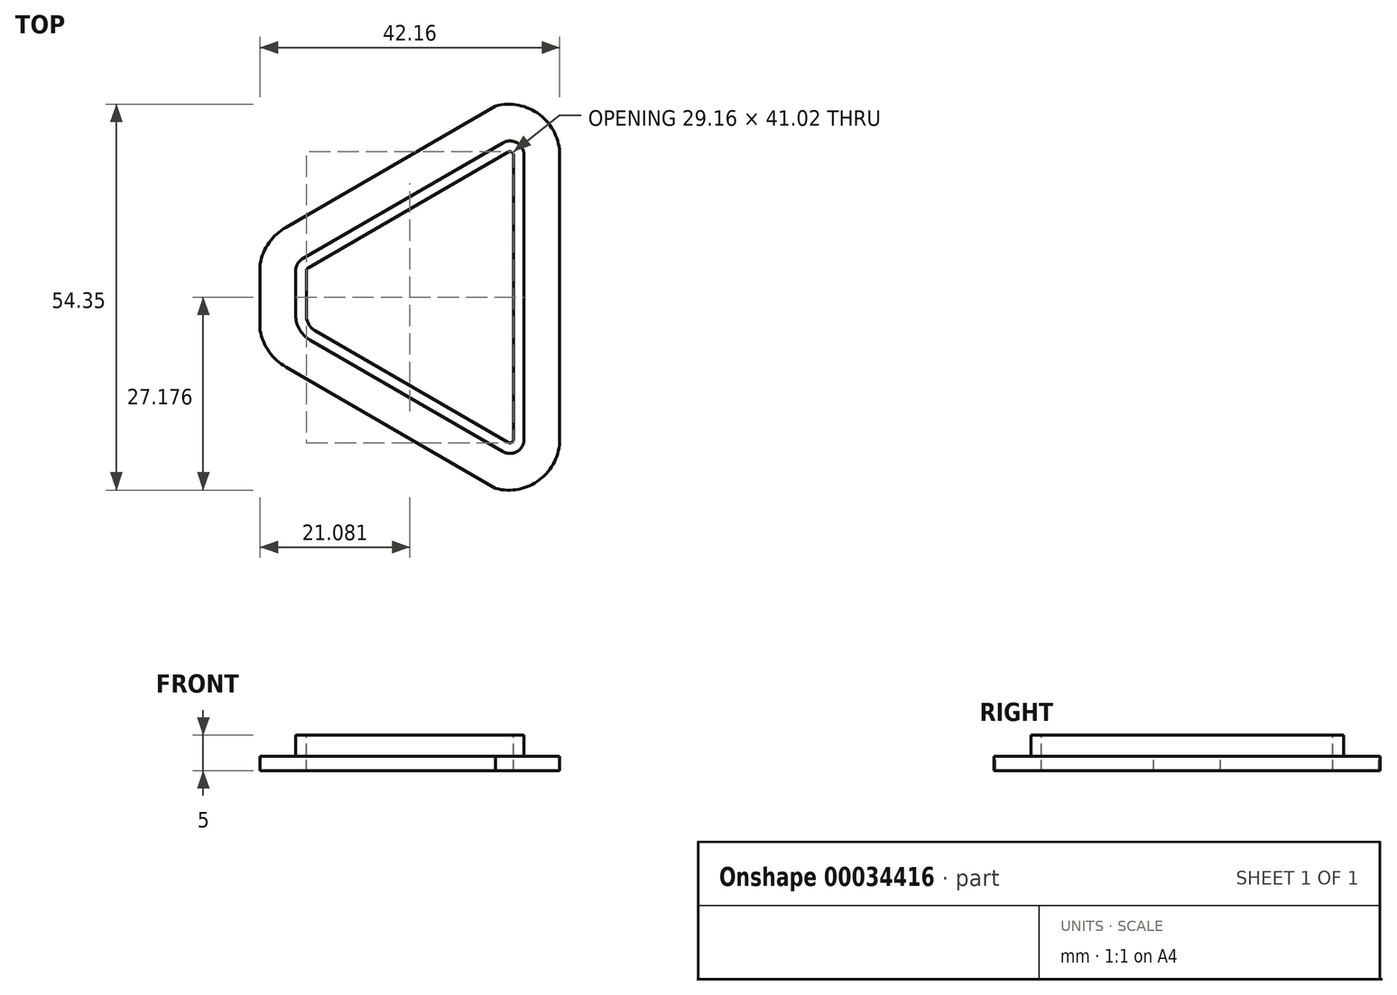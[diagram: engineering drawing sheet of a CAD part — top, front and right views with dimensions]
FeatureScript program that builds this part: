
annotation { "Feature Type Name" : "Feature", "Feature Type Description" : "" }
export const myFeature = defineFeature(function(context is Context, id is Id, definition is map)
    precondition{}
    {
        {
            var Q0;
            Q0=qCreatedBy(makeId("Top.planeOp"),FACE);
            var sketch = newSketch(context, id + "F0", { "sketchPlane" : qUnion([Q0])});
            skLineSegment(sketch, "E0", {"start": v(37.13, -26.3) * mm, "end": v(8.02, -9.43) * mm});
            skLineSegment(sketch, "E1", {"start": v(42.04, -2.18) * mm, "end": v(42.04, -22.18) * mm});
            skLineSegment(sketch, "E2", {"start": v(5.88, -6.57) * mm, "end": v(5.88, -2.18) * mm});
            skArc(sketch, "E3", {"start": v(5.88, -6.57) * mm, "mid": v(6.66, -8.22) * mm, "end": v(8.02, -9.43) * mm});
            skLineSegment(sketch, "E4", {"start": v(5.88, -2.18) * mm, "end": v(42.04, -2.18) * mm, "construction": true});
            skArc(sketch, "E5", {"start": v(37.13, -26.3) * mm, "mid": v(40.55, -25.38) * mm, "end": v(42.04, -22.18) * mm});
            skArc(sketch, "E6.MirrorCS", {"start": v(37.13, 21.92) * mm, "mid": v(40.55, 21.01) * mm, "end": v(42.04, 17.82) * mm});
            skLineSegment(sketch, "E7.MirrorCS", {"start": v(37.13, 21.92) * mm, "end": v(8.02, 5.06) * mm});
            skLineSegment(sketch, "E8.MirrorCS", {"start": v(42.04, -2.18) * mm, "end": v(42.04, 17.82) * mm});
            skLineSegment(sketch, "E9.MirrorCS", {"start": v(5.88, 2.2) * mm, "end": v(5.88, -2.18) * mm});
            skArc(sketch, "E10.MirrorCS", {"start": v(5.88, 2.2) * mm, "mid": v(6.66, 3.85) * mm, "end": v(8.02, 5.06) * mm});
            skSolve(sketch);
        }
        {
            var Q0;
            Q0=makeQuery(id+"F0.imprint","IMPRINT",FACE,{"disambiguationData":[TD([[makeQuery(id+"F0.imprint","IMPRINT",EDGE,{"derivedFrom":sQuery(id+"F0.wireOp",EDGE,"E0")}),-1.0]])]});
            var sketch = newSketch(context, id + "F1", { "sketchPlane" : qUnion([Q0])});
            skLineSegment(sketch, "E11.0.0", {"start": v(8.02, -9.43) * mm, "end": v(37.13, -26.3) * mm, "construction": true});
            skArc(sketch, "E11.0.1", {"start": v(37.13, -26.3) * mm, "mid": v(40.55, -25.38) * mm, "end": v(42.04, -22.18) * mm, "construction": true});
            skLineSegment(sketch, "E11.0.2", {"start": v(42.04, -22.18) * mm, "end": v(42.04, -2.18) * mm, "construction": true});
            skLineSegment(sketch, "E11.0.3", {"start": v(42.04, -2.18) * mm, "end": v(42.04, 17.82) * mm, "construction": true});
            skArc(sketch, "E11.0.4", {"start": v(42.04, 17.82) * mm, "mid": v(40.55, 21.01) * mm, "end": v(37.13, 21.92) * mm, "construction": true});
            skLineSegment(sketch, "E11.0.5", {"start": v(37.13, 21.92) * mm, "end": v(8.02, 5.06) * mm, "construction": true});
            skArc(sketch, "E11.0.6", {"start": v(8.02, 5.06) * mm, "mid": v(6.66, 3.85) * mm, "end": v(5.88, 2.2) * mm, "construction": true});
            skLineSegment(sketch, "E11.0.7", {"start": v(5.88, 2.2) * mm, "end": v(5.88, -2.18) * mm, "construction": true});
            skLineSegment(sketch, "E11.0.8", {"start": v(5.88, -2.18) * mm, "end": v(5.88, -6.57) * mm, "construction": true});
            skArc(sketch, "E11.0.9", {"start": v(5.88, -6.57) * mm, "mid": v(6.66, -8.22) * mm, "end": v(8.02, -9.43) * mm, "construction": true});
            skLineSegment(sketch, "E12.0", {"start": v(9.88, -8.2) * mm, "end": v(37.04, -23.92) * mm});
            skLineSegment(sketch, "E12.1", {"start": v(7.88, -2.18) * mm, "end": v(7.88, -4.74) * mm});
            skLineSegment(sketch, "E12.2", {"start": v(7.88, 1.52) * mm, "end": v(7.88, -2.18) * mm});
            skLineSegment(sketch, "E12.3", {"start": v(37.04, 19.56) * mm, "end": v(8.88, 3.25) * mm});
            skLineSegment(sketch, "E12.4", {"start": v(40.04, -2.18) * mm, "end": v(40.04, 17.82) * mm});
            skLineSegment(sketch, "E12.5", {"start": v(40.04, -22.2) * mm, "end": v(40.04, -2.18) * mm});
            skPoint(sketch, "E13.visualSharp", {"position": v(40.04, 21.3) * mm});
            skArc(sketch, "E13.filletArc", {"start": v(40.04, 17.82) * mm, "mid": v(39.04, 19.56) * mm, "end": v(37.04, 19.56) * mm});
            skPoint(sketch, "E14.visualSharp", {"position": v(40.04, -25.66) * mm});
            skArc(sketch, "E14.filletArc", {"start": v(37.04, -23.92) * mm, "mid": v(39.04, -23.92) * mm, "end": v(40.04, -22.2) * mm});
            skPoint(sketch, "E15.visualSharp", {"position": v(7.88, -7.04) * mm});
            skArc(sketch, "E15.filletArc", {"start": v(7.88, -4.74) * mm, "mid": v(8.42, -6.74) * mm, "end": v(9.88, -8.2) * mm});
            skPoint(sketch, "E16.visualSharp", {"position": v(7.88, 2.68) * mm});
            skArc(sketch, "E16.filletArc", {"start": v(8.88, 3.25) * mm, "mid": v(8.15, 2.52) * mm, "end": v(7.88, 1.52) * mm});
            skSolve(sketch);
        }
        {
            var Q0;
            Q0 = qSketchRegion(id + "F1", true);
            extrude(context, id + "F2", {"entities" : qUnion([Q0]), "depth" : 3 * mm});
        }
        {
            var Q0;
            Q0=makeQuery(id+"F0.imprint","IMPRINT",FACE,{"disambiguationData":[TD([[makeQuery(id+"F0.imprint","IMPRINT",EDGE,{"derivedFrom":sQuery(id+"F0.wireOp",EDGE,"E0")}),-1.0]])]});
            var sketch = newSketch(context, id + "F3", { "sketchPlane" : qUnion([Q0])});
            skArc(sketch, "E17.0", {"start": v(36.02, -29.11) * mm, "mid": v(42.24, -27.87) * mm, "end": v(45.04, -22.18) * mm});
            skLineSegment(sketch, "E17.1", {"start": v(45.04, -2.18) * mm, "end": v(45.04, -22.18) * mm});
            skLineSegment(sketch, "E17.2", {"start": v(45.04, -2.18) * mm, "end": v(45.04, 17.82) * mm});
            skArc(sketch, "E17.3", {"start": v(36.02, 24.75) * mm, "mid": v(42.24, 23.5) * mm, "end": v(45.04, 17.82) * mm});
            skLineSegment(sketch, "E17.4", {"start": v(36.02, 24.75) * mm, "end": v(6.51, 7.66) * mm});
            skLineSegment(sketch, "E17.5", {"start": v(36.02, -29.11) * mm, "end": v(6.51, -12.03) * mm});
            skArc(sketch, "E17.6", {"start": v(2.88, 2.52) * mm, "mid": v(4.13, 5.49) * mm, "end": v(6.51, 7.66) * mm});
            skLineSegment(sketch, "E17.7", {"start": v(2.88, 2.52) * mm, "end": v(2.88, -2.18) * mm});
            skLineSegment(sketch, "E17.8", {"start": v(2.88, -6.88) * mm, "end": v(2.88, -2.18) * mm});
            skArc(sketch, "E17.9", {"start": v(2.88, -6.88) * mm, "mid": v(4.13, -9.85) * mm, "end": v(6.51, -12.03) * mm});
            skSolve(sketch);
        }
        {
            var Q0;
            Q0 = qSketchRegion(id + "F3", true);
            extrude(context, id + "F4", {"entities" : qUnion([Q0]), "operationType" : NewBodyOperationType.ADD, "oppositeDirection" : true, "depth" : 2 * mm});
        }
        {
            var Q0;
            Q0=makeQuery(id+"F2.opExtrude","CAP_FACE",FACE,{"disambiguationData":[OSD([sQuery(id+"F1.wireOp",EDGE,"E12.0"),sQuery(id+"F1.wireOp",EDGE,"E12.1"),sQuery(id+"F1.wireOp",EDGE,"E12.2"),sQuery(id+"F1.wireOp",EDGE,"E12.3"),sQuery(id+"F1.wireOp",EDGE,"E12.4"),sQuery(id+"F1.wireOp",EDGE,"E12.5"),sQuery(id+"F1.wireOp",EDGE,"E13.filletArc"),sQuery(id+"F1.wireOp",EDGE,"E14.filletArc"),sQuery(id+"F1.wireOp",EDGE,"E15.filletArc"),sQuery(id+"F1.wireOp",EDGE,"E16.filletArc")])],"isStart":false});
            var sketch = newSketch(context, id + "F5", { "sketchPlane" : qUnion([Q0])});
            skLineSegment(sketch, "E18.0", {"start": v(9.38, 1.52) * mm, "end": v(9.38, -4.74) * mm});
            skArc(sketch, "E18.1", {"start": v(9.63, 1.96) * mm, "mid": v(9.45, 1.77) * mm, "end": v(9.38, 1.52) * mm});
            skLineSegment(sketch, "E18.2", {"start": v(37.79, 18.26) * mm, "end": v(9.63, 1.96) * mm});
            skArc(sketch, "E18.3", {"start": v(38.54, 17.82) * mm, "mid": v(38.29, 18.26) * mm, "end": v(37.79, 18.26) * mm});
            skLineSegment(sketch, "E18.4", {"start": v(38.54, -22.2) * mm, "end": v(38.54, 17.82) * mm});
            skArc(sketch, "E18.5", {"start": v(9.38, -4.74) * mm, "mid": v(9.72, -5.99) * mm, "end": v(10.63, -6.9) * mm});
            skArc(sketch, "E18.6", {"start": v(37.79, -22.62) * mm, "mid": v(38.29, -22.62) * mm, "end": v(38.54, -22.2) * mm});
            skLineSegment(sketch, "E18.7", {"start": v(10.63, -6.9) * mm, "end": v(37.79, -22.62) * mm});
            skSolve(sketch);
        }
        {
            var Q0;
            Q0 = qSketchRegion(id + "F5", true);
            extrude(context, id + "F6", {"entities" : qUnion([Q0]), "operationType" : NewBodyOperationType.REMOVE, "endBound" : BoundingType.THROUGH_ALL, "oppositeDirection" : true, "depth" : 25 * mm});
        }
    });
